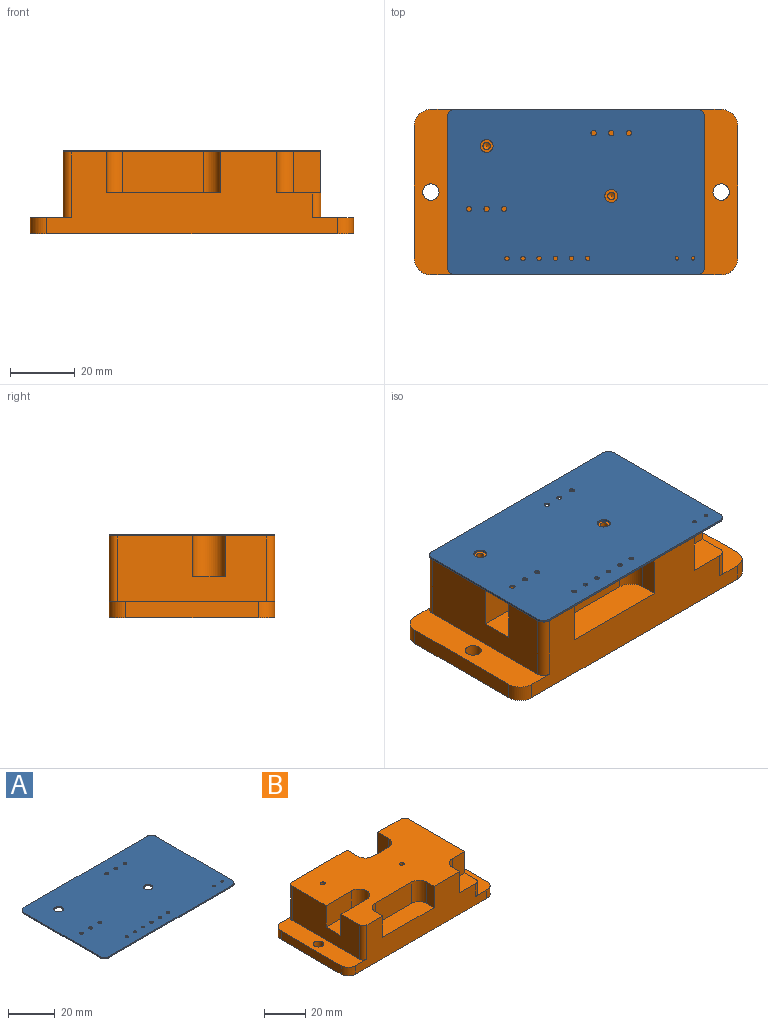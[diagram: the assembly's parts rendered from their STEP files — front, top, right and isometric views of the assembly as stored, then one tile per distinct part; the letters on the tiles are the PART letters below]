
ASSEMBLY  parts=2 mates=1
PART A: 26 faces, bbox 79.8x51.3x0.6 mm
  f0: cylinder r=2.54mm len=2.54mm, axis (0,0,-1), area 2.4mm2, adj f1,f7,f24,f25
  f1: plane 46.23x0.61mm, normal (-1,0,0), area 28.3mm2, adj f0,f2,f24,f25
  f2: cylinder r=2.54mm len=2.54mm, axis (0,0,-1), area 2.4mm2, adj f1,f3,f24,f25
  f3: plane 74.68x0.61mm, normal (0,1,0), area 45.7mm2, adj f2,f4,f24,f25
  f4: cylinder r=2.54mm len=2.54mm, axis (0,0,-1), area 2.4mm2, adj f3,f5,f24,f25
  f5: plane 46.23x0.61mm, normal (1,0,0), area 28.3mm2, adj f4,f6,f24,f25
  f6: cylinder r=2.54mm len=2.54mm, axis (0,0,-1), area 2.4mm2, adj f5,f7,f24,f25
  f7: plane 74.68x0.61mm, normal (0,-1,0), area 45.7mm2, adj f0,f6,f24,f25
  f8: cylinder r=0.7mm len=1.4mm, axis (0,0,-1), area 2.7mm2, adj f24,f25
  f9: cylinder r=0.7mm len=1.4mm, axis (0,0,-1), area 2.7mm2, adj f24,f25
  f10: cylinder r=0.7mm len=1.4mm, axis (0,0,-1), area 2.7mm2, adj f24,f25
  f11: cylinder r=0.7mm len=1.4mm, axis (0,0,-1), area 2.7mm2, adj f24,f25
  f12: cylinder r=0.83mm len=1.65mm, axis (0,0,-1), area 3.2mm2, adj f24,f25
  f13: cylinder r=0.83mm len=1.65mm, axis (0,0,-1), area 3.2mm2, adj f24,f25
  f14: cylinder r=0.83mm len=1.65mm, axis (0,0,-1), area 3.2mm2, adj f24,f25
  f15: cylinder r=2mm len=4mm, axis (0,0,-1), area 7.7mm2, adj f24,f25
  f16: cylinder r=0.7mm len=1.4mm, axis (0,0,-1), area 2.7mm2, adj f24,f25
  f17: cylinder r=0.7mm len=1.4mm, axis (0,0,-1), area 2.7mm2, adj f24,f25
  f18: cylinder r=0.55mm len=1.1mm, axis (0,0,-1), area 2.1mm2, adj f24,f25
  f19: cylinder r=0.55mm len=1.1mm, axis (0,0,-1), area 2.1mm2, adj f24,f25
  f20: cylinder r=0.83mm len=1.65mm, axis (0,0,-1), area 3.2mm2, adj f24,f25
  f21: cylinder r=0.83mm len=1.65mm, axis (0,0,-1), area 3.2mm2, adj f24,f25
  f22: cylinder r=2mm len=4mm, axis (0,0,-1), area 7.7mm2, adj f24,f25
  f23: cylinder r=0.83mm len=1.65mm, axis (0,0,-1), area 3.2mm2, adj f24,f25
  f24: plane 79.76x51.31mm, normal (0,0,-1), area 4037.5mm2, adj f0,f1,f2,f3,f4,f5,f6,f7
  f25: plane 79.76x51.31mm, normal (0,0,1), area 4037.5mm2, adj f0,f1,f2,f3,f4,f5,f6,f7
PART B: 44 faces, bbox 100.1x51.3x25.4 mm
  f0: plane 79.76x51.31mm, normal (0,0,1), area 3127.6mm2, adj f1,f2,f8,f9,f11,f13,f20,f21
  f1: plane 46.23x20.32mm, normal (-1,0,0), area 810.3mm2, adj f0,f3,f33,f34,f35,f40,f42
  f2: plane 89.92x25.4mm, normal (0,-1,0), area 1386.2mm2, adj f0,f3,f5,f7,f16,f17,f21,f22
  f3: plane 51.31x12.7mm, normal (0,0,1), area 492.7mm2, adj f1,f2,f4,f9,f14,f17,f19,f40
  f4: plane 41.15x5.08mm, normal (-1,0,0), area 209mm2, adj f3,f5,f17,f19
  f5: plane 100.08x51.31mm, normal (0,0,-1), area 5072mm2, adj f2,f4,f6,f9,f14,f15,f16,f17
  f6: plane 41.15x5.08mm, normal (1,0,0), area 209mm2, adj f5,f7,f16,f18
  f7: plane 51.31x12.7mm, normal (0,0,1), area 492.7mm2, adj f2,f6,f8,f9,f15,f16,f18,f41
  f8: plane 46.23x20.32mm, normal (1,0,0), area 842.6mm2, adj f0,f7,f36,f39,f41,f43
  f9: plane 89.92x25.4mm, normal (0,1,0), area 1706.4mm2, adj f0,f3,f5,f7,f18,f19,f29,f30
  f10: cone r=0mm half-angle=59deg, axis (0,0,1), area 4.7mm2, adj f11
  f11: cylinder r=1.13mm len=7.62mm, axis (0,0,1), area 54.1mm2, adj f0,f10
  f12: cone r=0mm half-angle=59deg, axis (0,0,1), area 4.7mm2, adj f13
  f13: cylinder r=1.13mm len=7.62mm, axis (0,0,1), area 54.1mm2, adj f0,f12
  f14: cylinder r=2.54mm len=5.08mm, axis (0,0,-1), area 81.1mm2, adj f3,f5
  f15: cylinder r=2.54mm len=5.08mm, axis (0,0,-1), area 81.1mm2, adj f5,f7
  f16: cylinder r=5.08mm len=5.08mm, axis (0,0,1), area 40.5mm2, adj f2,f5,f6,f7
  f17: cylinder r=5.08mm len=5.08mm, axis (0,0,-1), area 40.5mm2, adj f2,f3,f4,f5
  f18: cylinder r=5.08mm len=5.08mm, axis (0,0,-1), area 40.5mm2, adj f5,f6,f7,f9
  f19: cylinder r=5.08mm len=5.08mm, axis (0,0,1), area 40.5mm2, adj f3,f4,f5,f9
  f20: cylinder r=5.08mm len=12.7mm, axis (0,0,1), area 101.3mm2, adj f0,f21,f24,f25
  f21: plane 12.7x5.08mm, normal (1,0,0), area 64.5mm2, adj f0,f2,f20,f25
  f22: plane 12.7x5.08mm, normal (-1,0,0), area 64.5mm2, adj f0,f2,f23,f25
  f23: cylinder r=5.08mm len=12.7mm, axis (0,0,1), area 101.3mm2, adj f0,f22,f24,f25
  f24: plane 25x12.7mm, normal (0,-1,0), area 317.5mm2, adj f0,f20,f23,f25
  f25: plane 35.16x10.16mm, normal (0,0,1), area 346.1mm2, adj f2,f20,f21,f22,f23,f24
  f26: cylinder r=5.08mm len=12.7mm, axis (0,0,1), area 101.3mm2, adj f0,f27,f30,f31
  f27: plane 12.7x10.92mm, normal (0,1,0), area 138.7mm2, adj f0,f26,f28,f31
  f28: cylinder r=5.08mm len=12.7mm, axis (0,0,1), area 101.3mm2, adj f0,f27,f29,f31
  f29: plane 12.7x7.44mm, normal (-1,0,0), area 94.5mm2, adj f0,f9,f28,f31
  f30: plane 12.7x7.44mm, normal (1,0,0), area 94.5mm2, adj f0,f9,f26,f31
  f31: plane 21.08x12.52mm, normal (0,0,1), area 252.9mm2, adj f9,f26,f27,f28,f29,f30
  f32: cylinder r=5.08mm len=12.7mm, axis (0,0,1), area 202.7mm2, adj f0,f33,f34,f35
  f33: plane 17.65x12.7mm, normal (0,-1,0), area 224.2mm2, adj f0,f1,f32,f35
  f34: plane 17.65x12.7mm, normal (0,1,0), area 224.2mm2, adj f0,f1,f32,f35
  f35: plane 22.73x10.16mm, normal (0,0,1), area 219.9mm2, adj f1,f32,f33,f34
  f36: plane 12.7x8.6mm, normal (0,-1,0), area 109.2mm2, adj f0,f8,f37,f39
  f37: cylinder r=5.08mm len=12.7mm, axis (0,0,1), area 101.3mm2, adj f0,f36,f38,f39
  f38: plane 12.7x5.08mm, normal (1,0,0), area 64.5mm2, adj f0,f2,f37,f39
  f39: plane 13.68x10.16mm, normal (0,0,1), area 132mm2, adj f2,f8,f36,f37,f38,f41
  f40: cylinder r=2.54mm len=20.32mm, axis (0,0,-1), area 81.1mm2, adj f0,f1,f2,f3
  f41: cylinder r=2.54mm len=7.62mm, axis (0,0,1), area 30.4mm2, adj f2,f7,f8,f39
  f42: cylinder r=2.54mm len=20.32mm, axis (0,0,1), area 81.1mm2, adj f0,f1,f3,f9
  f43: cylinder r=2.54mm len=20.32mm, axis (0,0,-1), area 81.1mm2, adj f0,f7,f8,f9
PLACE A t=(-12.48,-26.53,4.37)mm
PLACE B t=(92.67,-1.13,-16.56)mm
MATE fastened A.f22 <-> B.f12  axis (0,0,-1) through (63.72,23.25,3.76)mm
